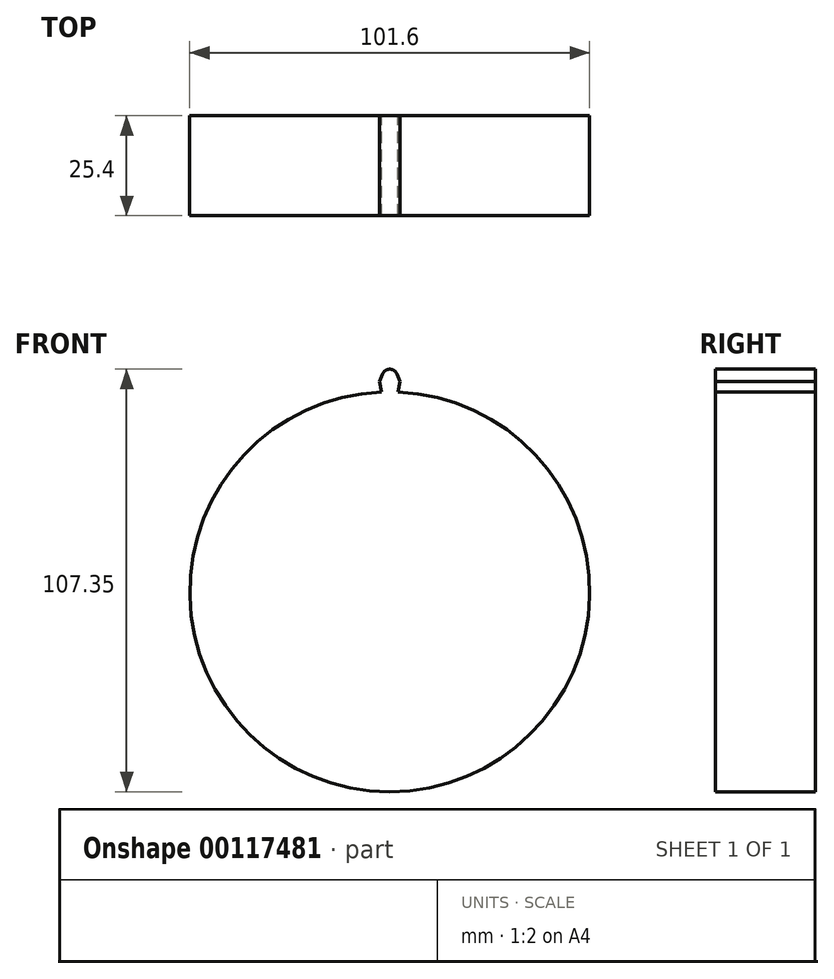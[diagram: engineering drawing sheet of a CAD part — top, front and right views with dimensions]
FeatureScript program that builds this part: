
annotation { "Feature Type Name" : "Feature", "Feature Type Description" : "" }
export const myFeature = defineFeature(function(context is Context, id is Id, definition is map)
    precondition{}
    {
        {
            var Q0;
            Q0=qCreatedBy(makeId("Front.planeOp"),FACE);
            var sketch = newSketch(context, id + "F0", { "sketchPlane" : qUnion([Q0])});
            skCircle(sketch, "E0", {"center": v(0, 0) * mm, "radius": 50.8 * mm});
            skSolve(sketch);
        }
        {
            var Q0;
            Q0 = qSketchRegion(id + "F0", true);
            extrude(context, id + "F1", {"entities" : qUnion([Q0]), "depth" : 25.4 * mm});
        }
        {
            var Q0;
            Q0=qCreatedBy(makeId("Front.planeOp"),FACE);
            var sketch = newSketch(context, id + "F2", { "sketchPlane" : qUnion([Q0])});
            skLineSegment(sketch, "E1", {"start": v(0, 50.88) * mm, "end": v(0, 56.04) * mm, "construction": true});
            skLineSegment(sketch, "E2", {"start": v(2.04, 50.71) * mm, "end": v(2.58, 53.37) * mm});
            skLineSegment(sketch, "E3.MirrorCS", {"start": v(-2.04, 50.71) * mm, "end": v(-2.58, 53.37) * mm});
            skLineSegment(sketch, "E4", {"start": v(2.58, 53.37) * mm, "end": v(1.8, 55.32) * mm});
            skLineSegment(sketch, "E5.MirrorCS", {"start": v(-2.58, 53.37) * mm, "end": v(-1.8, 55.32) * mm});
            skArc(sketch, "E6", {"start": v(-1.8, 55.32) * mm, "mid": v(0, 56.55) * mm, "end": v(1.8, 55.32) * mm});
            skArc(sketch, "E7", {"start": v(2.04, 50.71) * mm, "mid": v(0, 50.8) * mm, "end": v(-2.04, 50.71) * mm});
            skSolve(sketch);
        }
        {
            var Q0;
            Q0=makeQuery(id+"F2.imprint","IMPRINT",FACE,{"disambiguationData":[TD([[makeQuery(id+"F2.imprint","IMPRINT",EDGE,{"derivedFrom":sQuery(id+"F2.wireOp",EDGE,"E2")}),1.0]])]});
            extrude(context, id + "F3", {"entities" : qUnion([Q0]), "operationType" : NewBodyOperationType.ADD, "depth" : 25.4 * mm});
        }
        {
            var Q0;
            Q0=qCreatedBy(makeId("Right.planeOp"),FACE);
            var sketch = newSketch(context, id + "F4", { "sketchPlane" : qUnion([Q0])});
            skLineSegment(sketch, "E8", {"start": v(16.54, 0) * mm, "end": v(-60.19, 0) * mm, "construction": true});
            skSolve(sketch);
        }
        {
            var Q0;
            Q0=makeQuery(id+"F1.opExtrude","SWEPT_BODY",BODY,{"disambiguationData":[OSD([sQuery(id+"F0.wireOp",EDGE,"E0")])]});
            transform(context, id + "F5", {"entities" : qUnion([Q0]), "transformType" : TransformType.TRANSLATION_3D, "dx" : 0 * mm, "dy" : 0 * mm, "dz" : 0 * mm, "makeCopy" : true});
        }
        {
            var Q0;
            Q0=makeQuery(id+"F5.opPattern","COPY",BODY,{"derivedFrom":makeQuery(id+"F1.opExtrude","SWEPT_BODY",BODY,{"disambiguationData":[OSD([sQuery(id+"F0.wireOp",EDGE,"E0")])]}),"instanceName":"1"});
            deleteBodies(context, id + "F6", {"entities" : qUnion([Q0])});
        }
    });
